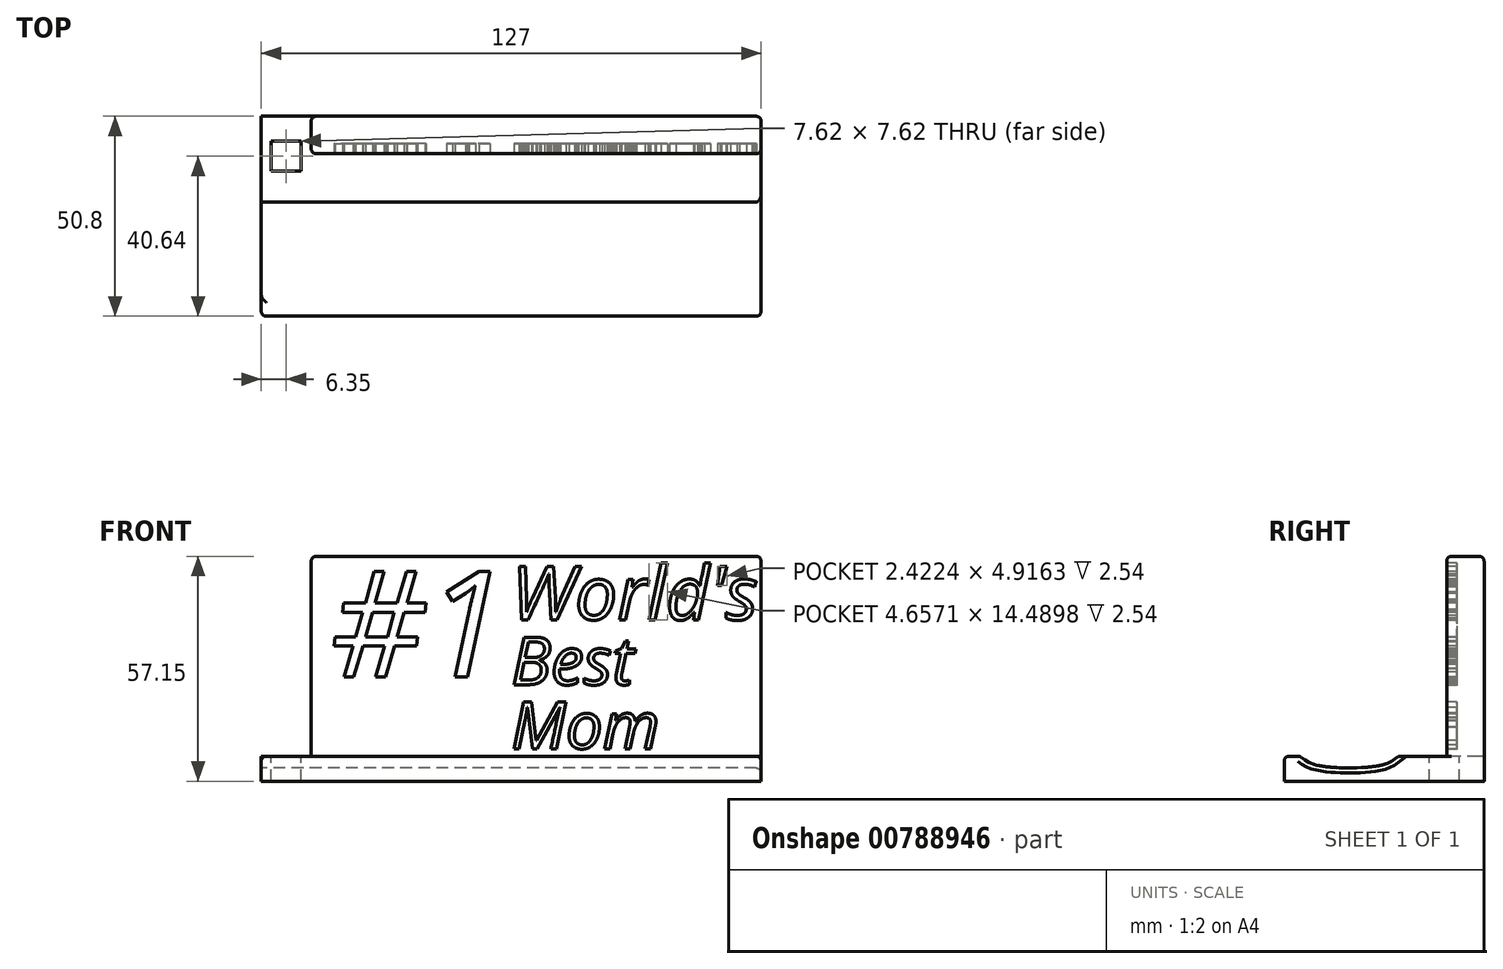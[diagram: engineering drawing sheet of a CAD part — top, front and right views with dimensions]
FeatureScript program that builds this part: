
annotation { "Feature Type Name" : "Feature", "Feature Type Description" : "" }
export const myFeature = defineFeature(function(context is Context, id is Id, definition is map)
    precondition{}
    {
        {
            var Q0;
            Q0=qCreatedBy(makeId("Top.planeOp"),FACE);
            var sketch = newSketch(context, id + "F0", { "sketchPlane" : qUnion([Q0])});
            skLineSegment(sketch, "E0.bottom", {"start": v(63.5, 25.4) * mm, "end": v(-63.5, 25.4) * mm});
            skLineSegment(sketch, "E0.top", {"start": v(63.5, -25.4) * mm, "end": v(-63.5, -25.4) * mm});
            skLineSegment(sketch, "E0.left", {"start": v(63.5, 25.4) * mm, "end": v(63.5, -25.4) * mm});
            skLineSegment(sketch, "E0.right", {"start": v(-63.5, 25.4) * mm, "end": v(-63.5, -25.4) * mm});
            skPoint(sketch, "E0.middle", {"position": v(0, 0) * mm});
            skSolve(sketch);
        }
        {
            var Q0;
            Q0=makeQuery(id+"F0.imprint","IMPRINT",FACE,{"disambiguationData":[TD([[makeQuery(id+"F0.imprint","IMPRINT",EDGE,{"derivedFrom":sQuery(id+"F0.wireOp",EDGE,"E0.bottom")}),1.0]])]});
            extrude(context, id + "F1", {"entities" : qUnion([Q0]), "depth" : 6.35 * mm, "offsetDistance" : 25.4 * mm});
        }
        {
            var Q0;
            Q0=makeQuery(id+"F1.opExtrude","CAP_FACE",FACE,{"disambiguationData":[OSD([sQuery(id+"F0.wireOp",EDGE,"E0.bottom"),sQuery(id+"F0.wireOp",EDGE,"E0.top"),sQuery(id+"F0.wireOp",EDGE,"E0.left"),sQuery(id+"F0.wireOp",EDGE,"E0.right")])],"isStart":false});
            var sketch = newSketch(context, id + "F2", { "sketchPlane" : qUnion([Q0])});
            skLineSegment(sketch, "E1.bottom", {"start": v(63.5, 25.4) * mm, "end": v(-50.8, 25.4) * mm});
            skLineSegment(sketch, "E1.top", {"start": v(63.5, 15.88) * mm, "end": v(-50.8, 15.87) * mm});
            skLineSegment(sketch, "E1.left", {"start": v(63.5, 25.4) * mm, "end": v(63.5, 15.88) * mm});
            skLineSegment(sketch, "E1.right", {"start": v(-50.8, 25.4) * mm, "end": v(-50.8, 15.87) * mm});
            skSolve(sketch);
        }
        {
            var Q0;
            Q0=makeQuery(id+"F2.imprint","IMPRINT",FACE,{"disambiguationData":[TD([[makeQuery(id+"F2.imprint","IMPRINT",EDGE,{"derivedFrom":sQuery(id+"F2.wireOp",EDGE,"E1.bottom")}),1.0]])]});
            extrude(context, id + "F3", {"entities" : qUnion([Q0]), "operationType" : NewBodyOperationType.ADD, "depth" : 50.8 * mm, "offsetDistance" : 25.4 * mm});
        }
        {
            var Q0;
            Q0=makeQuery(id+"F3.opExtrude","SWEPT_FACE",FACE,{"disambiguationData":[OSD([sQuery(id+"F2.wireOp",EDGE,"E1.top")])]});
            var sketch = newSketch(context, id + "F4", { "sketchPlane" : qUnion([Q0])});
            skText(sketch, "E2", { "text": "World\'s", "fontName": "OpenSans-Italic.ttf"});
            skText(sketch, "E3", { "text": "Best", "fontName": "OpenSans-Italic.ttf"});
            skText(sketch, "E4", { "text": "Mom", "fontName": "OpenSans-Italic.ttf"});
            skText(sketch, "E5", { "text": "#1", "fontName": "OpenSans-Italic.ttf"});
            const initialGuessF4  = {"E2": [0, 0.041, 1, 0, 0.01373], "E3": [0, 0.02453, 1, 0, 0.01215], "E4": [0, 0.00825, 1, 0, 0.01196], "E5": [-0.04616, 0.02645, 1, 0, 0.02702]};
            skSetInitialGuess(sketch, initialGuessF4);
            skSolve(sketch);
        }
        {
            var Q0;
            Q0 = qSketchRegion(id + "F4", true);
            extrude(context, id + "F5", {"entities" : qUnion([Q0]), "operationType" : NewBodyOperationType.REMOVE, "oppositeDirection" : true, "depth" : 2.54 * mm, "offsetDistance" : 25.4 * mm});
        }
        {
            var Q0;
            Q0=makeQuery(id+"F1.opExtrude","CAP_FACE",FACE,{"disambiguationData":[OSD([sQuery(id+"F0.wireOp",EDGE,"E0.bottom"),sQuery(id+"F0.wireOp",EDGE,"E0.top"),sQuery(id+"F0.wireOp",EDGE,"E0.left"),sQuery(id+"F0.wireOp",EDGE,"E0.right")])],"isStart":false});
            var sketch = newSketch(context, id + "F6", { "sketchPlane" : qUnion([Q0])});
            skLineSegment(sketch, "E6.bottom", {"start": v(-53.34, 19.05) * mm, "end": v(-60.96, 19.05) * mm});
            skLineSegment(sketch, "E6.top", {"start": v(-53.34, 11.43) * mm, "end": v(-60.96, 11.43) * mm});
            skLineSegment(sketch, "E6.left", {"start": v(-53.34, 19.05) * mm, "end": v(-53.34, 11.43) * mm});
            skLineSegment(sketch, "E6.right", {"start": v(-60.96, 19.05) * mm, "end": v(-60.96, 11.43) * mm});
            skPoint(sketch, "E6.middle", {"position": v(-57.15, 15.24) * mm});
            skSolve(sketch);
        }
        {
            var Q0;
            Q0=makeQuery(id+"F6.imprint","IMPRINT",FACE,{"disambiguationData":[TD([[makeQuery(id+"F6.imprint","IMPRINT",EDGE,{"derivedFrom":sQuery(id+"F6.wireOp",EDGE,"E6.bottom")}),1.0]])]});
            extrude(context, id + "F7", {"entities" : qUnion([Q0]), "operationType" : NewBodyOperationType.REMOVE, "oppositeDirection" : true, "depth" : 6.35 * mm, "offsetDistance" : 25.4 * mm});
        }
        {
            var Q0;
            Q0=makeQuery(id+"F3.opExtrude","CAP_EDGE",EDGE,{"disambiguationData":[OSD([sQuery(id+"F2.wireOp",EDGE,"E1.top")])],"isStart":false});
            var Q1;
            Q1=makeQuery(id+"F3.opExtrude","SWEPT_EDGE",EDGE,{"disambiguationData":[OSD([sQuery(id+"F2.wireOp",EDGE,"E1.top"),sQuery(id+"F2.wireOp",EDGE,"E1.right")])]});
            var Q2;
            Q2=makeQuery(id+"F3.opExtrude","SWEPT_EDGE",EDGE,{"disambiguationData":[OSD([sQuery(id+"F0.wireOp",EDGE,"E0.left"),sQuery(id+"F2.wireOp",EDGE,"E1.top"),sQuery(id+"F2.wireOp",EDGE,"E1.left")])]});
            var Q3;
            Q3=makeQuery(id+"F3.boolean.opBoolean","MERGE",EDGE,{"derivedFrom":[makeQuery(id+"F1.opExtrude","SWEPT_EDGE",EDGE,{"disambiguationData":[OSD([sQuery(id+"F0.wireOp",EDGE,"E0.bottom"),sQuery(id+"F0.wireOp",EDGE,"E0.left")])]}),makeQuery(id+"F3.opExtrude","SWEPT_EDGE",EDGE,{"disambiguationData":[OSD([sQuery(id+"F2.wireOp",EDGE,"E1.bottom"),sQuery(id+"F2.wireOp",EDGE,"E1.left")])]})]});
            var Q4;
            Q4=makeQuery(id+"F3.opExtrude","SWEPT_EDGE",EDGE,{"disambiguationData":[OSD([sQuery(id+"F0.wireOp",EDGE,"E0.bottom"),sQuery(id+"F2.wireOp",EDGE,"E1.bottom"),sQuery(id+"F2.wireOp",EDGE,"E1.right")])]});
            var Q5;
            Q5=makeQuery(id+"F3.opExtrude","CAP_EDGE",EDGE,{"disambiguationData":[OSD([sQuery(id+"F2.wireOp",EDGE,"E1.left")])],"isStart":false});
            var Q6;
            Q6=makeQuery(id+"F3.opExtrude","CAP_EDGE",EDGE,{"disambiguationData":[OSD([sQuery(id+"F2.wireOp",EDGE,"E1.right")])],"isStart":false});
            var Q7;
            Q7=makeQuery(id+"F3.opExtrude","CAP_EDGE",EDGE,{"disambiguationData":[OSD([sQuery(id+"F2.wireOp",EDGE,"E1.bottom")])],"isStart":false});
            var Q8;
            Q8=makeQuery(id+"F1.opExtrude","CAP_EDGE",EDGE,{"disambiguationData":[OSD([sQuery(id+"F0.wireOp",EDGE,"E0.top")])],"isStart":false});
            var Q9;
            {var subQ0=sQuery(id+"F9.wireOp",EDGE,"E7");var subQ1=sQuery(id+"F0.wireOp",EDGE,"E0.right");Q9=makeQuery(id+"F10.boolean.opBoolean","COPY",EDGE,{"derivedFrom":makeQuery(id+"F10.opExtrude","SWEPT_EDGE",EDGE,{"disambiguationData":[OSD([subQ1,subQ0]),TDD([makeQuery(id+"F9.imprint","INTERSECT",VERTEX,{"disambiguationData":[OD(1.0)],"derivedFrom":[makeQuery(id+"F1.opExtrude","CAP_EDGE",EDGE,{"disambiguationData":[OSD([subQ1])],"isStart":false}),subQ0]})])]})});}
            var Q10;
            Q10=makeQuery(id+"F10.boolean.opBoolean","COPY",EDGE,{"derivedFrom":makeQuery(id+"F10.opExtrude","CAP_EDGE",EDGE,{"disambiguationData":[OSD([sQuery(id+"F9.wireOp",EDGE,"E7")])],"isStart":true})});
            fillet(context, id + "F8", {"entities" : qUnion([Q0, Q1, Q2, Q3, Q4, Q5, Q6, Q7, Q8, Q9, Q10]), "radius" : 1.27 * mm, "tangentPropagation" : true, "allowEdgeOverflow" : false});
        }
        {
            var Q0;
            Q0=makeQuery(id+"F1.opExtrude","SWEPT_FACE",FACE,{"disambiguationData":[OSD([sQuery(id+"F0.wireOp",EDGE,"E0.right")])]});
            var sketch = newSketch(context, id + "F9", { "sketchPlane" : qUnion([Q0])});
            skFitSpline(sketch, "E7", {"points": [v(-3.63, 6.35) * mm, v(0.56, 4.14) * mm, v(17.21, 4.13) * mm, v(21.4, 6.35) * mm], "startDerivative": vector(11.55, -9.68) * mm, "endDerivative": vector(11.54, 9.75) * mm});
            skSolve(sketch);
        }
        {
            var Q0;
            {var subQ0=sQuery(id+"F9.wireOp",EDGE,"E7");Q0=makeQuery(id+"F9.imprint","IMPRINT",FACE,{"disambiguationData":[TD([[makeQuery(id+"F9.imprint","IMPRINT",EDGE,{"derivedFrom":subQ0}),1.0]])]});}
            extrude(context, id + "F10", {"entities" : qUnion([Q0]), "operationType" : NewBodyOperationType.REMOVE, "oppositeDirection" : true, "depth" : 141.73 * mm, "offsetDistance" : 25.4 * mm});
        }
        {
            var Q0;
            Q0=makeQuery(id+"F10.boolean.opBoolean","COPY",EDGE,{"derivedFrom":makeQuery(id+"F10.opExtrude","CAP_EDGE",EDGE,{"disambiguationData":[OSD([sQuery(id+"F9.wireOp",EDGE,"E7")])],"isStart":true})});
            var Q1;
            Q1=makeQuery(id+"F10.boolean.opBoolean","INTERSECT",EDGE,{"derivedFrom":[makeQuery(id+"F3.boolean.opBoolean","MERGE",FACE,{"derivedFrom":[makeQuery(id+"F1.opExtrude","SWEPT_FACE",FACE,{"disambiguationData":[OSD([sQuery(id+"F0.wireOp",EDGE,"E0.left")])]}),makeQuery(id+"F3.opExtrude","SWEPT_FACE",FACE,{"disambiguationData":[OSD([sQuery(id+"F2.wireOp",EDGE,"E1.left")])]})]}),makeQuery(id+"F10.opExtrude","SWEPT_FACE",FACE,{"disambiguationData":[OSD([sQuery(id+"F9.wireOp",EDGE,"E7")])]})]});
            var Q2;
            {var subQ0=sQuery(id+"F0.wireOp",EDGE,"E0.right");var subQ1=sQuery(id+"F0.wireOp",EDGE,"E0.top");Q2=makeQuery(id+"F10.boolean.opBoolean","SPLIT",EDGE,{"disambiguationData":[TD([makeQuery(id+"F8.opFillet","BLEND_FACE",FACE,{"disambiguationData":[OSD([subQ1])]})])],"derivedFrom":makeQuery(id+"F1.opExtrude","CAP_EDGE",EDGE,{"disambiguationData":[OSD([subQ0])],"isStart":false})});}
            var Q3;
            {var subQ0=sQuery(id+"F9.wireOp",EDGE,"E7");var subQ1=sQuery(id+"F0.wireOp",EDGE,"E0.right");Q3=makeQuery(id+"F10.boolean.opBoolean","COPY",EDGE,{"derivedFrom":makeQuery(id+"F10.opExtrude","SWEPT_EDGE",EDGE,{"disambiguationData":[OSD([subQ1,subQ0]),TDD([makeQuery(id+"F9.imprint","INTERSECT",VERTEX,{"disambiguationData":[OD(1.0)],"derivedFrom":[makeQuery(id+"F1.opExtrude","CAP_EDGE",EDGE,{"disambiguationData":[OSD([subQ1])],"isStart":false}),subQ0]})])]})});}
            var Q4;
            {var subQ0=sQuery(id+"F9.wireOp",EDGE,"E7");var subQ1=sQuery(id+"F0.wireOp",EDGE,"E0.right");Q4=makeQuery(id+"F10.boolean.opBoolean","COPY",EDGE,{"derivedFrom":makeQuery(id+"F10.opExtrude","SWEPT_EDGE",EDGE,{"disambiguationData":[OSD([subQ1,subQ0]),TDD([makeQuery(id+"F9.imprint","INTERSECT",VERTEX,{"disambiguationData":[OD(0.0)],"derivedFrom":[makeQuery(id+"F1.opExtrude","CAP_EDGE",EDGE,{"disambiguationData":[OSD([subQ1])],"isStart":false}),subQ0]})])]})});}
            var Q5;
            {var subQ0=sQuery(id+"F0.wireOp",EDGE,"E0.top");var subQ1=sQuery(id+"F0.wireOp",EDGE,"E0.left");Q5=makeQuery(id+"F10.boolean.opBoolean","SPLIT",EDGE,{"disambiguationData":[TD([makeQuery(id+"F8.opFillet","BLEND_FACE",FACE,{"disambiguationData":[OSD([subQ0])]})])],"derivedFrom":makeQuery(id+"F1.opExtrude","CAP_EDGE",EDGE,{"disambiguationData":[OSD([subQ1])],"isStart":false})});}
            fillet(context, id + "F11", {"entities" : qUnion([Q0, Q1, Q2, Q3, Q4, Q5]), "radius" : 1.27 * mm, "tangentPropagation" : true, "allowEdgeOverflow" : false});
        }
    });
